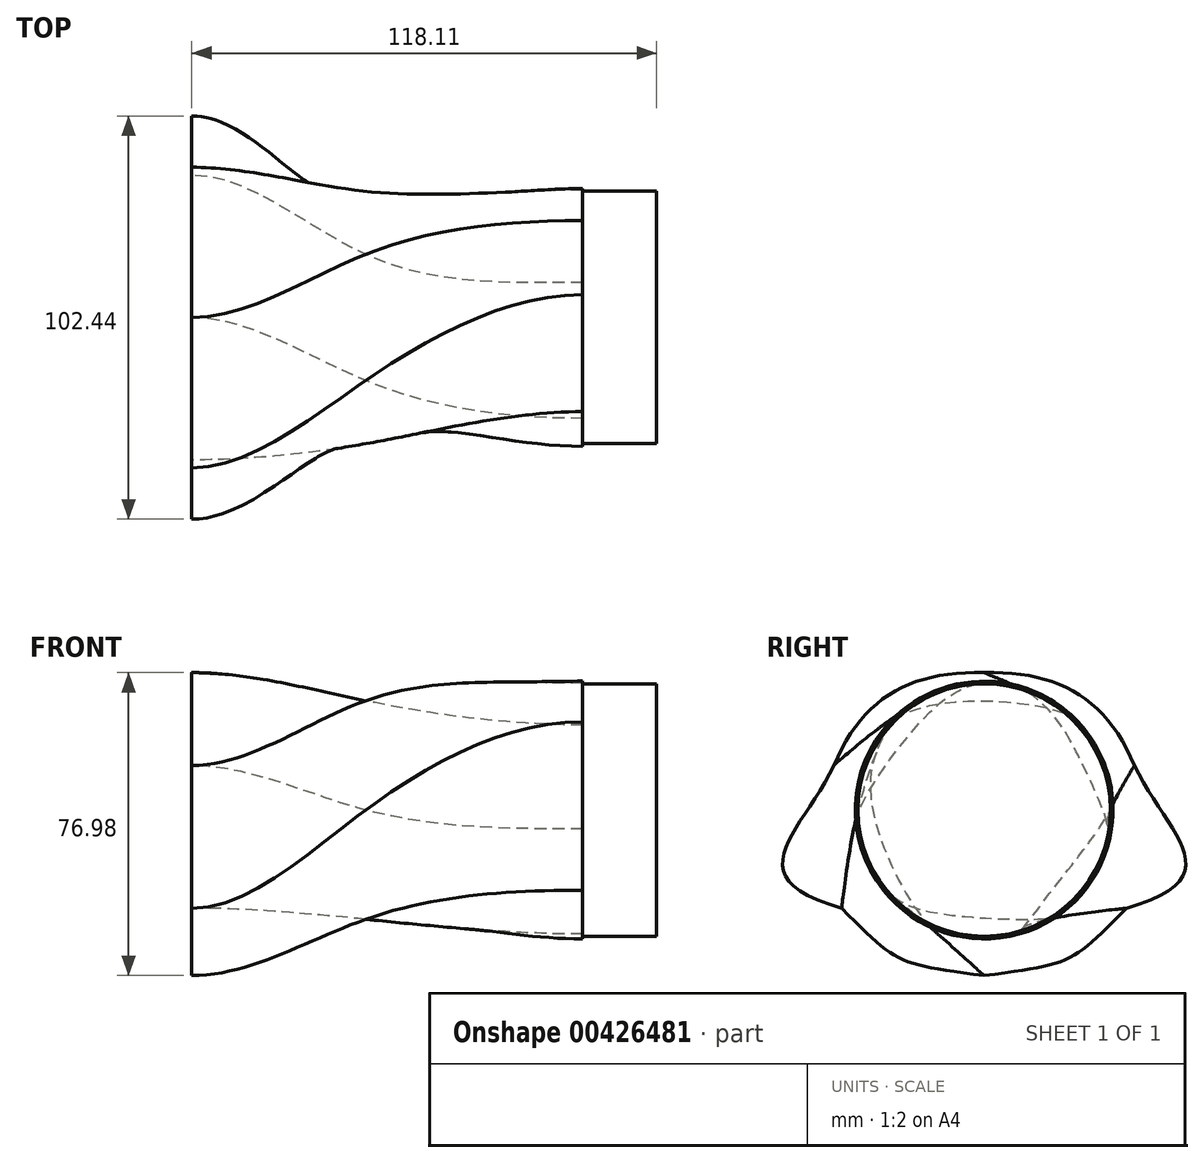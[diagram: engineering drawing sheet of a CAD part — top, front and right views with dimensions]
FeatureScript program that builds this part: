
annotation { "Feature Type Name" : "Feature", "Feature Type Description" : "" }
export const myFeature = defineFeature(function(context is Context, id is Id, definition is map)
    precondition{}
    {
        {
            var Q0;
            Q0=qCreatedBy(makeId("Right.planeOp"),FACE);
            var sketch = newSketch(context, id + "F0", { "sketchPlane" : qUnion([Q0])});
            skCircle(sketch, "E0", {"center": v(0, 0) * mm, "radius": 32.06 * mm});
            skSolve(sketch);
        }
        {
            var Q0;
            Q0=makeQuery(id+"F0.imprint","IMPRINT",FACE,{"disambiguationData":[TD([[makeQuery(id+"F0.imprint","IMPRINT",EDGE,{"derivedFrom":sQuery(id+"F0.wireOp",EDGE,"E0")}),1.0]])]});
            extrude(context, id + "F1", {"entities" : qUnion([Q0]), "depth" : 18.8 * mm});
        }
        {
            var Q0;
            Q0=qCreatedBy(makeId("Right.planeOp"),FACE);
            var sketch = newSketch(context, id + "F2", { "sketchPlane" : qUnion([Q0])});
            skArc(sketch, "E1", {"start": v(24.6, 21.62) * mm, "mid": v(16.09, 28.52) * mm, "end": v(5.78, 32.23) * mm});
            skArc(sketch, "E2", {"start": v(5.78, 32.23) * mm, "mid": v(-10.31, 31.08) * mm, "end": v(-23.9, 22.38) * mm});
            skArc(sketch, "E3", {"start": v(-23.9, 22.38) * mm, "mid": v(-32.72, 1.32) * mm, "end": v(-25.63, -20.38) * mm});
            skArc(sketch, "E4", {"start": v(-25.63, -20.38) * mm, "mid": v(-10.04, -31.17) * mm, "end": v(8.9, -31.5) * mm});
            skArc(sketch, "E5", {"start": v(8.9, -31.5) * mm, "mid": v(24.6, -21.62) * mm, "end": v(32.4, -4.8) * mm});
            skArc(sketch, "E6", {"start": v(32.4, -4.8) * mm, "mid": v(31.4, 9.27) * mm, "end": v(24.6, 21.62) * mm});
            skSolve(sketch);
        }
        {
            var Q0;
            Q0=qCreatedBy(makeId("Right.planeOp"),FACE);
            cPlane(context, id + "F3", {"entities" : qUnion([Q0]), "cplaneType" : CPlaneType.OFFSET, "offset" : 55.12 * mm, "oppositeDirection" : true, "width" : 152.4 * mm, "height" : 152.4 * mm});
        }
        {
            var Q0;
            Q0=qCreatedBy(id+"F3.planeOp",FACE);
            cPlane(context, id + "F4", {"entities" : qUnion([Q0]), "cplaneType" : CPlaneType.OFFSET, "offset" : 44.2 * mm, "oppositeDirection" : true, "width" : 152.4 * mm, "height" : 152.4 * mm});
        }
        {
            var Q0;
            Q0=qCreatedBy(id+"F3.planeOp",FACE);
            var sketch = newSketch(context, id + "F5", { "sketchPlane" : qUnion([Q0])});
            skCircle(sketch, "E7.cCircle", {"center": v(0, 0) * mm, "radius": 27.77 * mm, "construction": true});
            skLineSegment(sketch, "E7.0", {"start": v(16.03, 27.77) * mm, "end": v(-16.03, 27.77) * mm});
            skLineSegment(sketch, "E7.1", {"start": v(32.07, 0) * mm, "end": v(16.03, 27.77) * mm});
            skLineSegment(sketch, "E7.2", {"start": v(16.03, -27.77) * mm, "end": v(32.07, 0) * mm});
            skLineSegment(sketch, "E7.3", {"start": v(-16.03, -27.77) * mm, "end": v(16.03, -27.77) * mm});
            skLineSegment(sketch, "E7.4", {"start": v(-32.07, 0) * mm, "end": v(-16.03, -27.77) * mm});
            skLineSegment(sketch, "E7.5", {"start": v(-16.03, 27.77) * mm, "end": v(-32.07, 0) * mm});
            skPoint(sketch, "E7.0.midPoint", {"position": v(0, 27.77) * mm});
            skSolve(sketch);
        }
        {
            var Q0;
            Q0=qCreatedBy(id+"F4.planeOp",FACE);
            var sketch = newSketch(context, id + "F6", { "sketchPlane" : qUnion([Q0])});
            skFitSpline(sketch, "E8", {"points": [v(0, 34.9) * mm, v(38.18, 11.32) * mm], "startDerivative": vector(56.48, 1.33) * mm, "endDerivative": vector(22.02, -52.05) * mm});
            skFitSpline(sketch, "E9", {"points": [v(38.18, 11.32) * mm, v(36.18, -24.93) * mm], "startDerivative": vector(24.69, -51.38) * mm, "endDerivative": vector(-83.12, -23.36) * mm});
            skFitSpline(sketch, "E10", {"points": [v(36.18, -24.93) * mm, v(0, -42.06) * mm], "startDerivative": vector(-42.04, -42.7) * mm, "endDerivative": vector(-66.49, -8.67) * mm});
            skLineSegment(sketch, "E11", {"start": v(0, 34.9) * mm, "end": v(0, -42.06) * mm, "construction": true});
            skFitSpline(sketch, "E12.MirrorCS", {"points": [v(-36.18, -24.93) * mm, v(0, -42.06) * mm], "startDerivative": vector(42.04, -42.7) * mm, "endDerivative": vector(66.49, -8.67) * mm});
            skFitSpline(sketch, "E13.MirrorCS", {"points": [v(-38.18, 11.32) * mm, v(-36.18, -24.93) * mm], "startDerivative": vector(-24.69, -51.38) * mm, "endDerivative": vector(83.12, -23.36) * mm});
            skFitSpline(sketch, "E14.MirrorCS", {"points": [v(0, 34.9) * mm, v(-38.18, 11.32) * mm], "startDerivative": vector(-56.48, 1.33) * mm, "endDerivative": vector(-22.02, -52.05) * mm});
            skSolve(sketch);
        }
        {
            var Q1;
            Q1=makeQuery(id+"F2.imprint","IMPRINT",FACE,{"disambiguationData":[TD([[makeQuery(id+"F2.imprint","IMPRINT",EDGE,{"derivedFrom":sQuery(id+"F2.wireOp",EDGE,"E1")}),1.0]])]});
            var Q2;
            Q2=makeQuery(id+"F5.imprint","IMPRINT",FACE,{"disambiguationData":[TD([[makeQuery(id+"F5.imprint","IMPRINT",EDGE,{"derivedFrom":sQuery(id+"F5.wireOp",EDGE,"E7.0")}),1.0]])]});
            var Q3;
            Q3=makeQuery(id+"F6.imprint","IMPRINT",FACE,{"disambiguationData":[TD([[makeQuery(id+"F6.imprint","IMPRINT",EDGE,{"derivedFrom":sQuery(id+"F6.wireOp",EDGE,"E8")}),-1.0]])]});
            var Q4;
            Q4=sQuery(id+"F5.wireOp",VERTEX,"E7.1.start");
            var Q5;
            Q5=sQuery(id+"F6.wireOp",VERTEX,"E9.start");
            var Q6;
            Q6=sQuery(id+"F2.wireOp",VERTEX,"E1.start");
            var Q7;
            Q7=sQuery(id+"F2.wireOp",VERTEX,"E2.start");
            var Q8;
            Q8=sQuery(id+"F5.wireOp",VERTEX,"E7.0.midPoint");
            var Q9;
            Q9=sQuery(id+"F6.wireOp",VERTEX,"E14.MirrorCS.start");
            loft(context, id + "F7", {"operationType" : NewBodyOperationType.ADD, "startCondition" : LoftEndDerivativeType.NORMAL_TO_PROFILE, "startMagnitude" : 1, "endCondition" : LoftEndDerivativeType.NORMAL_TO_PROFILE, "endMagnitude" : 1, "sheetProfilesArray" : [{ "sheetProfileEntities" : qUnion([Q1]) }, { "sheetProfileEntities" : qUnion([Q2]) }, { "sheetProfileEntities" : qUnion([Q3]) }], "connections" : [{ "connectionEntities" : qUnion([Q4, Q5, Q6, Q7, Q8, Q9]), "connectionEdgeQueries" : qUnion([]), "connectionEdgeParameters" : [] }]});
        }
    });
